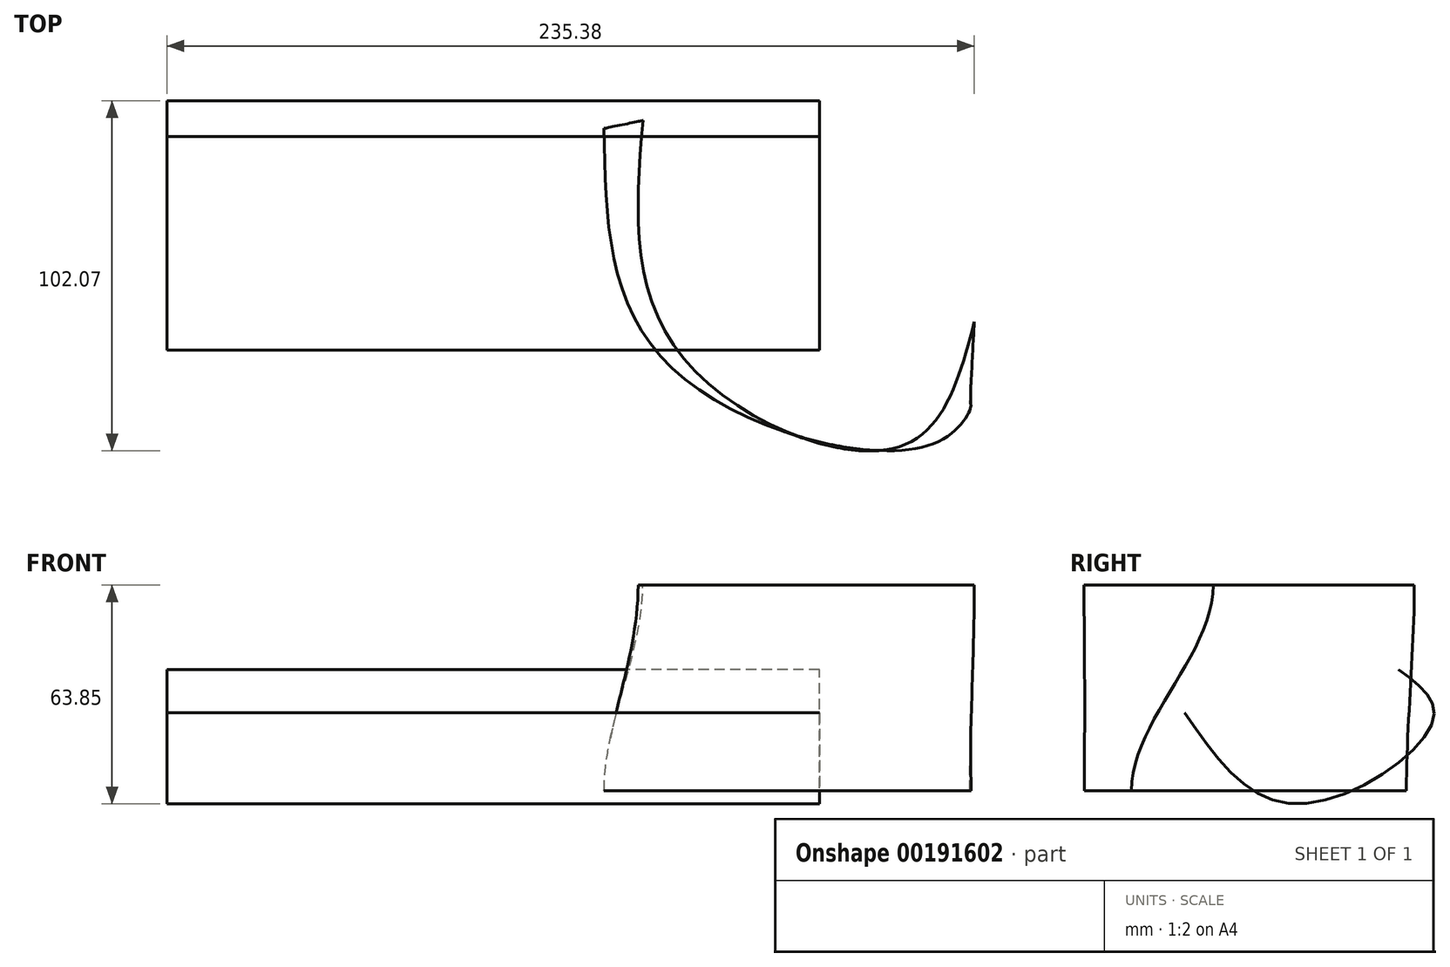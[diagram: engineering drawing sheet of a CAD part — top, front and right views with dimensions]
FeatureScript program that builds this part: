
annotation { "Feature Type Name" : "Feature", "Feature Type Description" : "" }
export const myFeature = defineFeature(function(context is Context, id is Id, definition is map)
    precondition{}
    {
        {
            var Q0;
            Q0=qCreatedBy(makeId("Top.planeOp"),FACE);
            var sketch = newSketch(context, id + "F0", { "sketchPlane" : qUnion([Q0])});
            skFitSpline(sketch, "E0", {"points": [v(-62.74, 49.73) * mm, v(-43.33, -19.75) * mm, v(33.69, -41.94) * mm, v(44.2, -30.97) * mm, v(43.89, -30.44) * mm], "startDerivative": vector(2.73, -201.22) * mm, "endDerivative": vector(-12.25, 9.43) * mm});
            skSolve(sketch);
        }
        {
            var Q0;
            Q0=qCreatedBy(makeId("Top.planeOp"),FACE);
            cPlane(context, id + "F1", {"entities" : qUnion([Q0]), "cplaneType" : CPlaneType.OFFSET, "offset" : 60 * mm, "width" : 150 * mm, "height" : 150 * mm});
        }
        {
            var Q0;
            Q0=qCreatedBy(id+"F1.planeOp",FACE);
            var sketch = newSketch(context, id + "F2", { "sketchPlane" : qUnion([Q0])});
            skFitSpline(sketch, "E1", {"points": [v(-51.44, 52.03) * mm, v(-40.55, -16.06) * mm, v(23.41, -42.98) * mm, v(45.18, -6.56) * mm], "startDerivative": vector(-16.76, -205.3) * mm, "endDerivative": vector(44.97, 170.85) * mm});
            skSolve(sketch);
        }
        {
            var Q0;
            Q0=sQuery(id+"F0.wireOp",VERTEX,"E0.2.internal");
            var Q1;
            Q1=sQuery(id+"F2.wireOp",VERTEX,"E1.2.internal");
            var Q2;
            Q2=sQuery(id+"F0.wireOp",EDGE,"E0");
            var Q3;
            Q3=sQuery(id+"F2.wireOp",EDGE,"E1");
            loft(context, id + "F3", {"bodyType" : ToolBodyType.SURFACE, "startCondition" : LoftEndDerivativeType.NORMAL_TO_PROFILE, "startMagnitude" : 1, "endCondition" : LoftEndDerivativeType.NORMAL_TO_PROFILE, "endMagnitude" : 1, "sheetProfilesArray" : [{ "sheetProfileEntities" : qUnion([Q0]) }, { "sheetProfileEntities" : qUnion([Q1]) }], "wireProfilesArray" : [{ "wireProfileEntities" : qUnion([Q2]) }, { "wireProfileEntities" : qUnion([Q3]) }]});
        }
        {
            var Q0;
            Q0=qCreatedBy(makeId("Right.planeOp"),FACE);
            var sketch = newSketch(context, id + "F4", { "sketchPlane" : qUnion([Q0])});
            skFitSpline(sketch, "E2", {"points": [v(-14.92, 22.67) * mm, v(18.19, -3.85) * mm, v(57.58, 20.8) * mm, v(47.42, 35.27) * mm], "startDerivative": vector(74.12, -107.4) * mm, "endDerivative": vector(-72.8, 52.6) * mm});
            skSolve(sketch);
        }
        {
            var Q0;
            Q0=sQuery(id+"F4.wireOp",EDGE,"E2");
            extrude(context, id + "F5", {"bodyType" : ToolBodyType.SURFACE, "surfaceEntities" : qUnion([Q0]), "oppositeDirection" : true, "depth" : 190.2 * mm});
        }
        {
            var Q0;
            Q0=qCreatedBy(makeId("Right.planeOp"),FACE);
            var sketch = newSketch(context, id + "F6", { "sketchPlane" : qUnion([Q0])});
            skLineSegment(sketch, "E3", {"start": v(-59.26, 66.76) * mm, "end": v(74.24, 0) * mm});
            skSolve(sketch);
        }
        {
            var Q0;
            Q0=sQuery(id+"F6.wireOp",EDGE,"E3");
            var Q1;
            Q1=qCreatedBy(makeId("Right.planeOp"),FACE);
            cPlane(context, id + "F7", {"entities" : qUnion([Q0, Q1]), "cplaneType" : CPlaneType.LINE_ANGLE, "offset" : 25 * mm, "angle" : 90 * degree, "width" : 150 * mm, "height" : 150 * mm});
        }
    });
